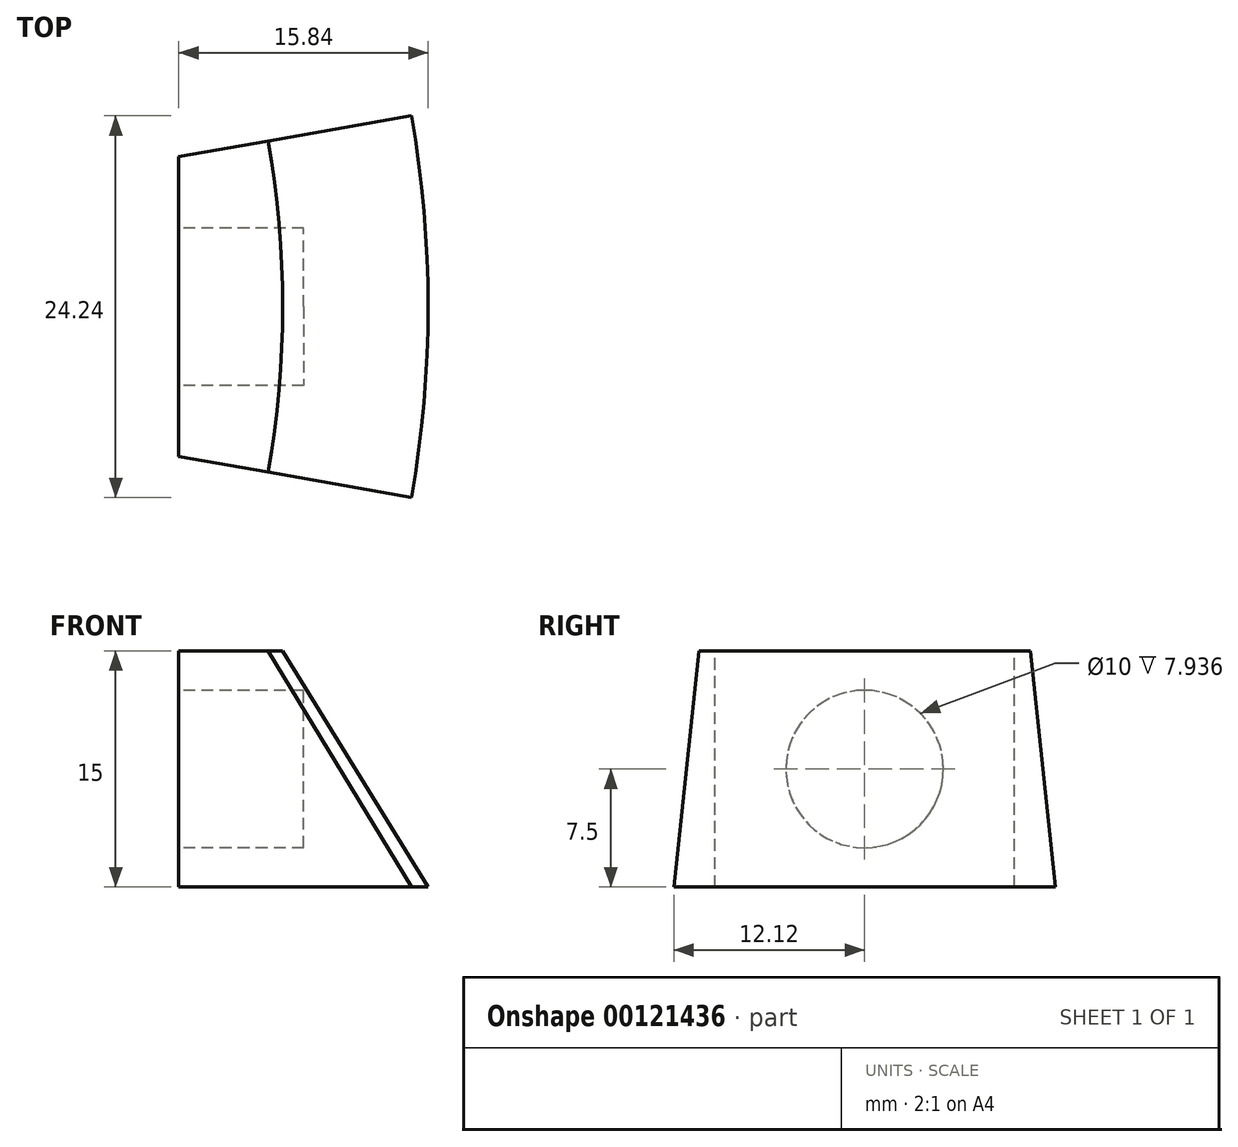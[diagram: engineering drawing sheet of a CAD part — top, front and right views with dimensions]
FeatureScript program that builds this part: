
annotation { "Feature Type Name" : "Feature", "Feature Type Description" : "" }
export const myFeature = defineFeature(function(context is Context, id is Id, definition is map)
    precondition{}
    {
        {
            var Q0;
            Q0=qCreatedBy(makeId("Front.planeOp"),FACE);
            var sketch = newSketch(context, id + "F0", { "sketchPlane" : qUnion([Q0])});
            skLineSegment(sketch, "E0", {"start": v(0, 0) * mm, "end": v(0, 25.25) * mm});
            skLineSegment(sketch, "E1.0", {"start": v(60.55, 15) * mm, "end": v(69.8, 0) * mm});
            skLineSegment(sketch, "E2", {"start": v(69.8, 0) * mm, "end": v(54.8, 0) * mm});
            skLineSegment(sketch, "E3", {"start": v(54.8, 0) * mm, "end": v(54.8, 15) * mm});
            skLineSegment(sketch, "E4", {"start": v(54.8, 15) * mm, "end": v(60.55, 15) * mm});
            skSolve(sketch);
        }
        {
            var Q0;
            Q0=makeQuery(id+"F0.imprint","IMPRINT",FACE,{"disambiguationData":[TD([[makeQuery(id+"F0.imprint","IMPRINT",EDGE,{"derivedFrom":sQuery(id+"F0.wireOp",EDGE,"E1.0")}),-1.0]])]});
            var Q1;
            Q1=sQuery(id+"F0.wireOp",EDGE,"E0");
            revolve(context, id + "F5", {"entities" : qUnion([Q0]), "axis" : qUnion([Q1]), "revolveType" : RevolveType.TWO_DIRECTIONS, "angle" : 10 * degree, "angleBack" : 350 * degree});
        }
        {
            var Q0;
            Q0=qCreatedBy(makeId("Right.planeOp"),FACE);
            var sketch = newSketch(context, id + "F1", { "sketchPlane" : qUnion([Q0])});
            skCircle(sketch, "E5", {"center": v(0, 7.5) * mm, "radius": 5 * mm});
            skSolve(sketch);
        }
        {
            var Q0;
            Q0=makeQuery(id+"F5.opRevolve","SWEPT_FACE",FACE,{"disambiguationData":[OSD([sQuery(id+"F0.wireOp",EDGE,"E4")])]});
            var sketch = newSketch(context, id + "F2", { "sketchPlane" : qUnion([Q0])});
            skLineSegment(sketch, "E6", {"start": v(53.96, 9.52) * mm, "end": v(53.96, -9.52) * mm});
            skLineSegment(sketch, "E7", {"start": v(53.96, -9.52) * mm, "end": v(54.8, -9.66) * mm});
            skPoint(sketch, "E7.endSnap0", {"position": v(54.8, 0) * mm});
            skLineSegment(sketch, "E8", {"start": v(54.8, 9.66) * mm, "end": v(53.96, 9.52) * mm});
            skLineSegment(sketch, "E9", {"start": v(54.8, 9.66) * mm, "end": v(56.5, 0) * mm});
            skLineSegment(sketch, "E10", {"start": v(56.5, 0) * mm, "end": v(54.8, -9.66) * mm});
            skSolve(sketch);
        }
        {
            var Q0;
            Q0 = qSketchRegion(id + "F2", true);
            extrude(context, id + "F3", {"entities" : qUnion([Q0]), "operationType" : NewBodyOperationType.ADD, "oppositeDirection" : true, "depth" : 15 * mm});
        }
        {
            var Q0;
            Q0 = qSketchRegion(id + "F1", true);
            extrude(context, id + "F4", {"entities" : qUnion([Q0]), "operationType" : NewBodyOperationType.REMOVE, "depth" : 61.9 * mm});
        }
    });
